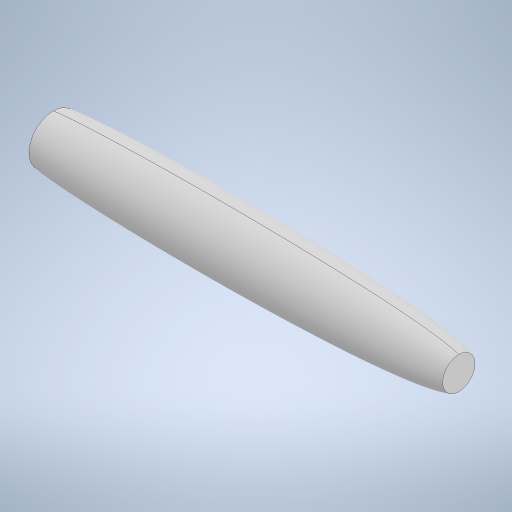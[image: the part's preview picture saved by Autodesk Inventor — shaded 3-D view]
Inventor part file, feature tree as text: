
AUTODESK INVENTOR PART (.ipt)
format: ipt  version: 2023 (Build 270158030, 158C)  size: 280,576 bytes
history: native  units: mm
features: revolve x1, sketch x1
ambient origin geometry x8: Origin, YZ Plane, XZ Plane, XY Plane, X Axis, Y Axis, Z Axis, Center Point
bodies: Solid1 (feature_tree)
feature tree (2):
  revolve  "Revolution1"  [1 undecoded]
  sketch  "Sketch3"  dims[d1=100.0mm d2=6.0mm d3=4.0mm d4=7.0mm d5=8.0mm d6=8.0mm d7=38.0mm d8=20.0mm d9=43.0mm d10=50.0mm d11=90.0deg]
note: 1 required parameter value undecoded (feature->parameter linkage not recoverable at this tier; creation-order binding heuristic only, values carry confidence <= 0.55)
